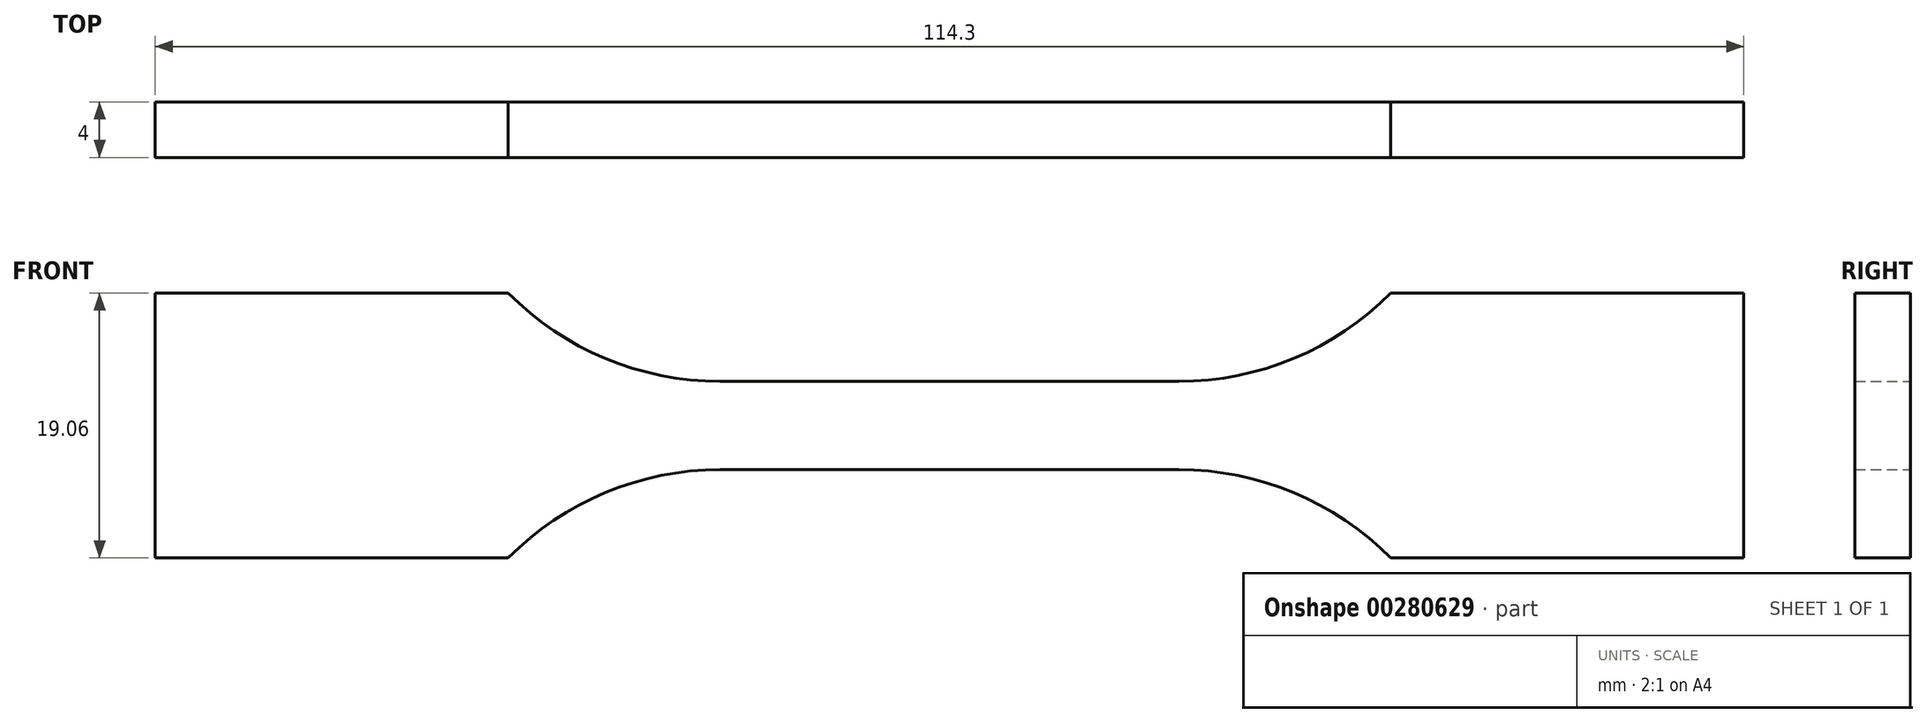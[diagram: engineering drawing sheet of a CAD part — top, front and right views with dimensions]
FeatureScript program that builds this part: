
annotation { "Feature Type Name" : "Feature", "Feature Type Description" : "" }
export const myFeature = defineFeature(function(context is Context, id is Id, definition is map)
    precondition{}
    {
        {
            var Q0;
            Q0=qCreatedBy(makeId("Front.planeOp"),FACE);
            var sketch = newSketch(context, id + "F0", { "sketchPlane" : qUnion([Q0])});
            skLineSegment(sketch, "E0", {"start": v(0, 3.18) * mm, "end": v(16.51, 3.18) * mm});
            skArc(sketch, "E1", {"start": v(16.51, 3.18) * mm, "mid": v(24.77, 4.83) * mm, "end": v(31.75, 9.53) * mm});
            skLineSegment(sketch, "E2", {"start": v(31.75, 9.53) * mm, "end": v(57.15, 9.53) * mm});
            skLineSegment(sketch, "E3", {"start": v(57.15, 9.53) * mm, "end": v(57.15, 0) * mm});
            skLineSegment(sketch, "E4.MirrorCS", {"start": v(0, -3.17) * mm, "end": v(16.51, -3.17) * mm});
            skLineSegment(sketch, "E5.MirrorCS", {"start": v(57.15, -9.53) * mm, "end": v(57.15, 0) * mm});
            skLineSegment(sketch, "E6.MirrorCS", {"start": v(31.75, -9.53) * mm, "end": v(57.15, -9.53) * mm});
            skArc(sketch, "E7.MirrorCS", {"start": v(16.51, -3.18) * mm, "mid": v(24.77, -4.83) * mm, "end": v(31.75, -9.53) * mm});
            skArc(sketch, "E8.MirrorCS", {"start": v(-16.51, -3.18) * mm, "mid": v(-24.77, -4.83) * mm, "end": v(-31.75, -9.53) * mm});
            skLineSegment(sketch, "E9.MirrorCS", {"start": v(-31.75, -9.53) * mm, "end": v(-57.15, -9.53) * mm});
            skArc(sketch, "E10.MirrorCS", {"start": v(-16.51, 3.18) * mm, "mid": v(-24.77, 4.83) * mm, "end": v(-31.75, 9.53) * mm});
            skLineSegment(sketch, "E11.MirrorCS", {"start": v(-31.75, 9.53) * mm, "end": v(-57.15, 9.53) * mm});
            skLineSegment(sketch, "E12.MirrorCS", {"start": v(-57.15, -9.53) * mm, "end": v(-57.15, 0) * mm});
            skLineSegment(sketch, "E13.MirrorCS", {"start": v(0, -3.17) * mm, "end": v(-16.51, -3.17) * mm});
            skLineSegment(sketch, "E14.MirrorCS", {"start": v(-57.15, 9.53) * mm, "end": v(-57.15, 0) * mm});
            skLineSegment(sketch, "E15.MirrorCS", {"start": v(0, 3.18) * mm, "end": v(-16.51, 3.18) * mm});
            skSolve(sketch);
        }
        {
            var Q0;
            Q0=makeQuery(id+"F0.imprint","IMPRINT",FACE,{"disambiguationData":[TD([[makeQuery(id+"F0.imprint","IMPRINT",EDGE,{"derivedFrom":sQuery(id+"F0.wireOp",EDGE,"E0")}),-1.0]])]});
            extrude(context, id + "F1", {"entities" : qUnion([Q0]), "endBound" : BoundingType.SYMMETRIC, "depth" : 4 * mm});
        }
    });
